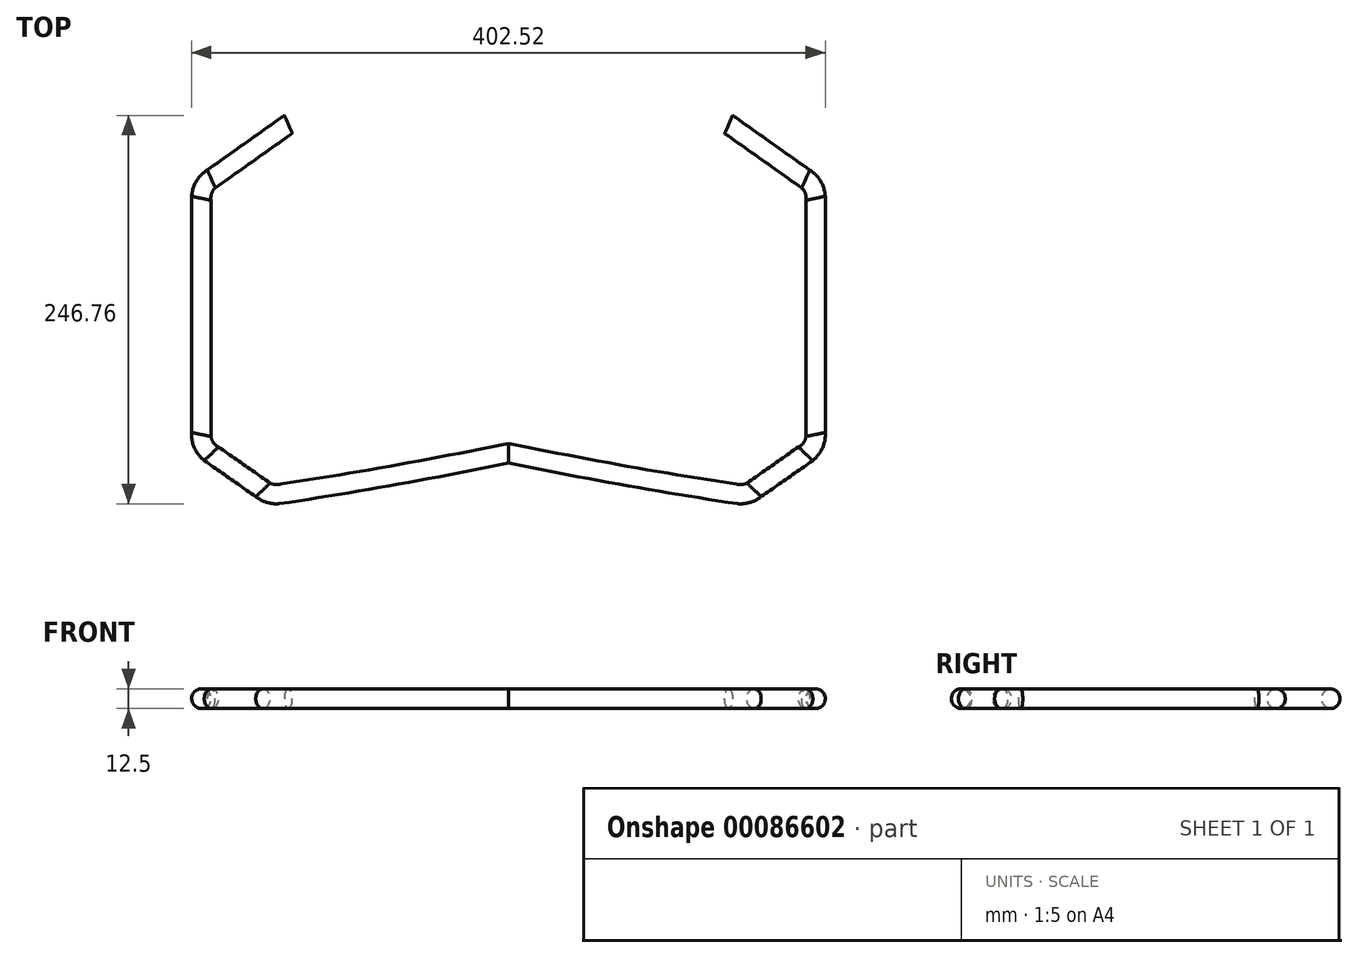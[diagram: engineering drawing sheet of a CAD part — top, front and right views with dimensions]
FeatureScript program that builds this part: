
annotation { "Feature Type Name" : "Feature", "Feature Type Description" : "" }
export const myFeature = defineFeature(function(context is Context, id is Id, definition is map)
    precondition{}
    {
        {
            var Q0;
            Q0=qCreatedBy(makeId("Top.planeOp"),FACE);
            var sketch = newSketch(context, id + "F0", { "sketchPlane" : qUnion([Q0])});
            skLineSegment(sketch, "E0", {"start": v(-139.82, 189.06) * mm, "end": v(-188.78, 154.37) * mm});
            skLineSegment(sketch, "E1", {"start": v(-195.1, 142.13) * mm, "end": v(-195.1, -7.87) * mm});
            skLineSegment(sketch, "E2", {"start": v(-188.7, -20.16) * mm, "end": v(-155.94, -43.1) * mm});
            skPoint(sketch, "E3.visualSharp", {"position": v(-195.1, 149.89) * mm});
            skArc(sketch, "E3.filletArc", {"start": v(-188.78, 154.37) * mm, "mid": v(-193.43, 149.02) * mm, "end": v(-195.1, 142.13) * mm});
            skPoint(sketch, "E4.visualSharp", {"position": v(-151.03, -46.54) * mm});
            skArc(sketch, "E4.filletArc", {"start": v(-155.94, -43.1) * mm, "mid": v(-150.76, -45.41) * mm, "end": v(-145.1, -45.64) * mm});
            skPoint(sketch, "E5.visualSharp", {"position": v(-195.1, -15.68) * mm});
            skArc(sketch, "E5.filletArc", {"start": v(-195.1, -7.87) * mm, "mid": v(-193.4, -14.8) * mm, "end": v(-188.7, -20.16) * mm});
            skArc(sketch, "E6", {"start": v(-145.1, -45.64) * mm, "mid": v(-72.37, -33.7) * mm, "end": v(0, -19.79) * mm});
            skLineSegment(sketch, "E7", {"start": v(0, 0) * mm, "end": v(0, -48.17) * mm});
            skPoint(sketch, "E8.orphan", {"position": v(-398.68, -71.66) * mm});
            skArc(sketch, "E9.MirrorCS", {"start": v(155.94, -43.1) * mm, "mid": v(150.76, -45.41) * mm, "end": v(145.1, -45.64) * mm});
            skArc(sketch, "E10.MirrorCS", {"start": v(188.78, 154.37) * mm, "mid": v(193.43, 149.02) * mm, "end": v(195.1, 142.13) * mm});
            skArc(sketch, "E11.MirrorCS", {"start": v(195.1, -7.87) * mm, "mid": v(193.4, -14.8) * mm, "end": v(188.7, -20.16) * mm});
            skLineSegment(sketch, "E12.MirrorCS", {"start": v(195.1, 142.13) * mm, "end": v(195.1, -7.87) * mm});
            skLineSegment(sketch, "E13.MirrorCS", {"start": v(139.82, 189.06) * mm, "end": v(188.78, 154.37) * mm});
            skArc(sketch, "E14.MirrorCS", {"start": v(145.1, -45.64) * mm, "mid": v(72.37, -33.7) * mm, "end": v(0, -19.79) * mm});
            skLineSegment(sketch, "E15.MirrorCS", {"start": v(188.7, -20.16) * mm, "end": v(155.94, -43.1) * mm});
            skPoint(sketch, "E16.MirrorP", {"position": v(195.1, 149.89) * mm});
            skPoint(sketch, "E17.MirrorP", {"position": v(151.03, -46.54) * mm});
            skPoint(sketch, "E18.MirrorP", {"position": v(195.1, -15.68) * mm});
            skSolve(sketch);
        }
        {
            var Q0;
            Q0=qCreatedBy(makeId("Right.planeOp"),FACE);
            var sketch = newSketch(context, id + "F1", { "sketchPlane" : qUnion([Q0])});
            skCircle(sketch, "E19", {"center": v(-19.79, 0) * mm, "radius": 6.25 * mm});
            skSolve(sketch);
        }
        {
            var Q0;
            Q0=makeQuery(id+"F1.imprint","IMPRINT",FACE,{"disambiguationData":[TD([[makeQuery(id+"F1.imprint","IMPRINT",EDGE,{"derivedFrom":sQuery(id+"F1.wireOp",EDGE,"E19")}),1.0]])]});
            var Q1;
            Q1=sQuery(id+"F0.wireOp",EDGE,"E14.MirrorCS");
            var Q2;
            Q2=sQuery(id+"F0.wireOp",EDGE,"E9.MirrorCS");
            var Q3;
            Q3=sQuery(id+"F0.wireOp",EDGE,"E15.MirrorCS");
            var Q4;
            Q4=sQuery(id+"F0.wireOp",EDGE,"E11.MirrorCS");
            var Q5;
            Q5=sQuery(id+"F0.wireOp",EDGE,"E12.MirrorCS");
            var Q6;
            Q6=sQuery(id+"F0.wireOp",EDGE,"E10.MirrorCS");
            var Q7;
            Q7=sQuery(id+"F0.wireOp",EDGE,"E13.MirrorCS");
            sweep(context, id + "F2", {"profiles" : qUnion([Q0]), "path" : qUnion([Q1, Q2, Q3, Q4, Q5, Q6, Q7])});
        }
        {
            var Q0;
            Q0=makeQuery(id+"F2.opSweep","SWEPT_BODY",BODY,{"disambiguationData":[OSD([sQuery(id+"F0.wireOp",EDGE,"E13.MirrorCS"),sQuery(id+"F1.wireOp",EDGE,"E19")])]});
            var Q1;
            Q1=qCreatedBy(makeId("Right.planeOp"),FACE);
            mirror(context, id + "F3", {"operationType" : NewBodyOperationType.ADD, "entities" : qUnion([Q0]), "mirrorPlane" : qUnion([Q1])});
        }
    });
